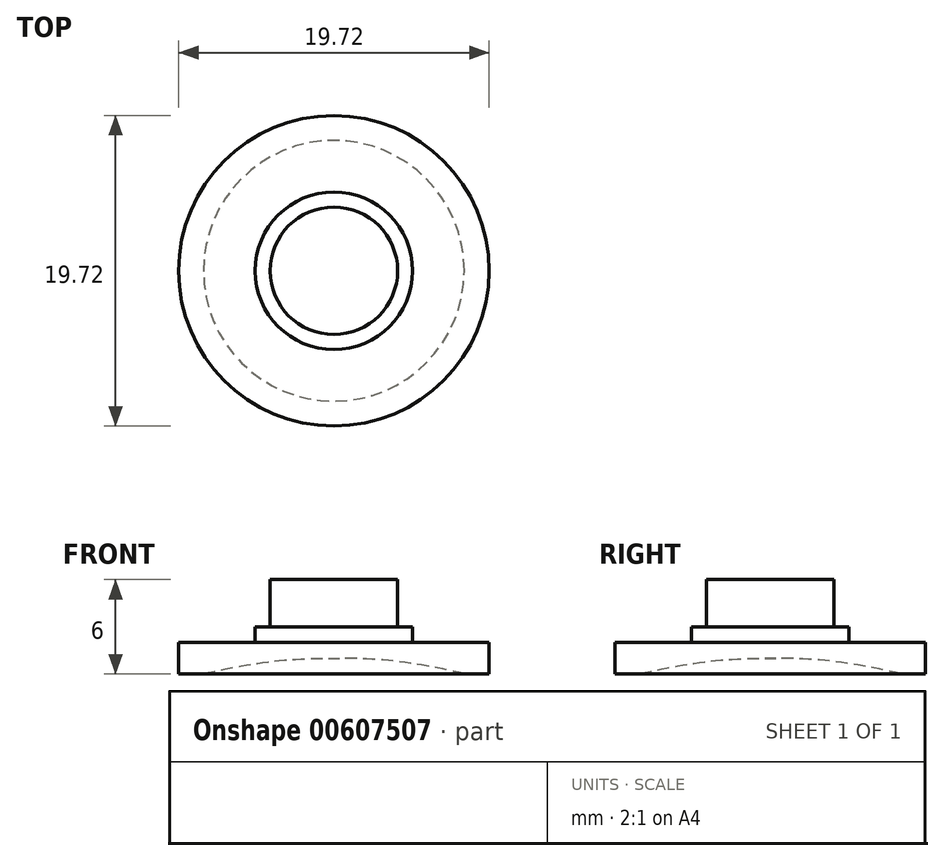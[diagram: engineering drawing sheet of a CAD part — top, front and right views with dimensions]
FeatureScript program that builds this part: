
annotation { "Feature Type Name" : "Feature", "Feature Type Description" : "" }
export const myFeature = defineFeature(function(context is Context, id is Id, definition is map)
    precondition{}
    {
        {
            var Q0;
            Q0=qCreatedBy(makeId("Top.planeOp"),FACE);
            var sketch = newSketch(context, id + "F0", { "sketchPlane" : qUnion([Q0])});
            skCircle(sketch, "E0", {"center": v(0, 0) * mm, "radius": 9.86 * mm});
            skSolve(sketch);
        }
        {
            var Q0;
            Q0 = qSketchRegion(id + "F0", true);
            extrude(context, id + "F1", {"entities" : qUnion([Q0]), "depth" : 2 * mm, "offsetDistance" : 25 * mm});
        }
        {
            var Q0;
            Q0=makeQuery(id+"F1.opExtrude","CAP_FACE",FACE,{"disambiguationData":[OSD([sQuery(id+"F0.wireOp",EDGE,"E0")])],"isStart":false});
            var sketch = newSketch(context, id + "F2", { "sketchPlane" : qUnion([Q0])});
            skCircle(sketch, "E1", {"center": v(0, 0) * mm, "radius": 5 * mm});
            skSolve(sketch);
        }
        {
            var Q0;
            Q0 = qSketchRegion(id + "F2", true);
            extrude(context, id + "F3", {"entities" : qUnion([Q0]), "operationType" : NewBodyOperationType.ADD, "depth" : 1 * mm, "offsetDistance" : 25 * mm});
        }
        {
            var Q0;
            Q0=makeQuery(id+"F3.opExtrude","CAP_FACE",FACE,{"disambiguationData":[OSD([sQuery(id+"F2.wireOp",EDGE,"E1")])],"isStart":false});
            var sketch = newSketch(context, id + "F4", { "sketchPlane" : qUnion([Q0])});
            skCircle(sketch, "E2", {"center": v(0, 0) * mm, "radius": 4.05 * mm});
            skSolve(sketch);
        }
        {
            var Q0;
            Q0 = qSketchRegion(id + "F4", true);
            extrude(context, id + "F5", {"entities" : qUnion([Q0]), "operationType" : NewBodyOperationType.ADD, "depth" : 3 * mm, "offsetDistance" : 25 * mm});
        }
        {
            var Q0;
            Q0=makeQuery(id+"F1.opExtrude","CAP_FACE",FACE,{"disambiguationData":[OSD([sQuery(id+"F0.wireOp",EDGE,"E0")])],"isStart":true});
            var sketch = newSketch(context, id + "F6", { "sketchPlane" : qUnion([Q0])});
            skCircle(sketch, "E3", {"center": v(0, 0) * mm, "radius": 8.28 * mm});
            skSolve(sketch);
        }
        {
            var Q0;
            Q0 = qSketchRegion(id + "F6", true);
            extrude(context, id + "F7", {"entities" : qUnion([Q0]), "operationType" : NewBodyOperationType.REMOVE, "oppositeDirection" : true, "depth" : 1 * mm, "offsetDistance" : 25 * mm});
        }
        {
            var Q0;
            Q0=makeQuery(id+"F7.boolean.opBoolean","COPY",EDGE,{"derivedFrom":makeQuery(id+"F7.opExtrude","CAP_EDGE",EDGE,{"disambiguationData":[OSD([sQuery(id+"F6.wireOp",EDGE,"E3")])],"isStart":false})});
            fillet(context, id + "F8", {"entities" : qUnion([Q0]), "radius" : 32 * mm, "tangentPropagation" : true, "allowEdgeOverflow" : false});
        }
    });
